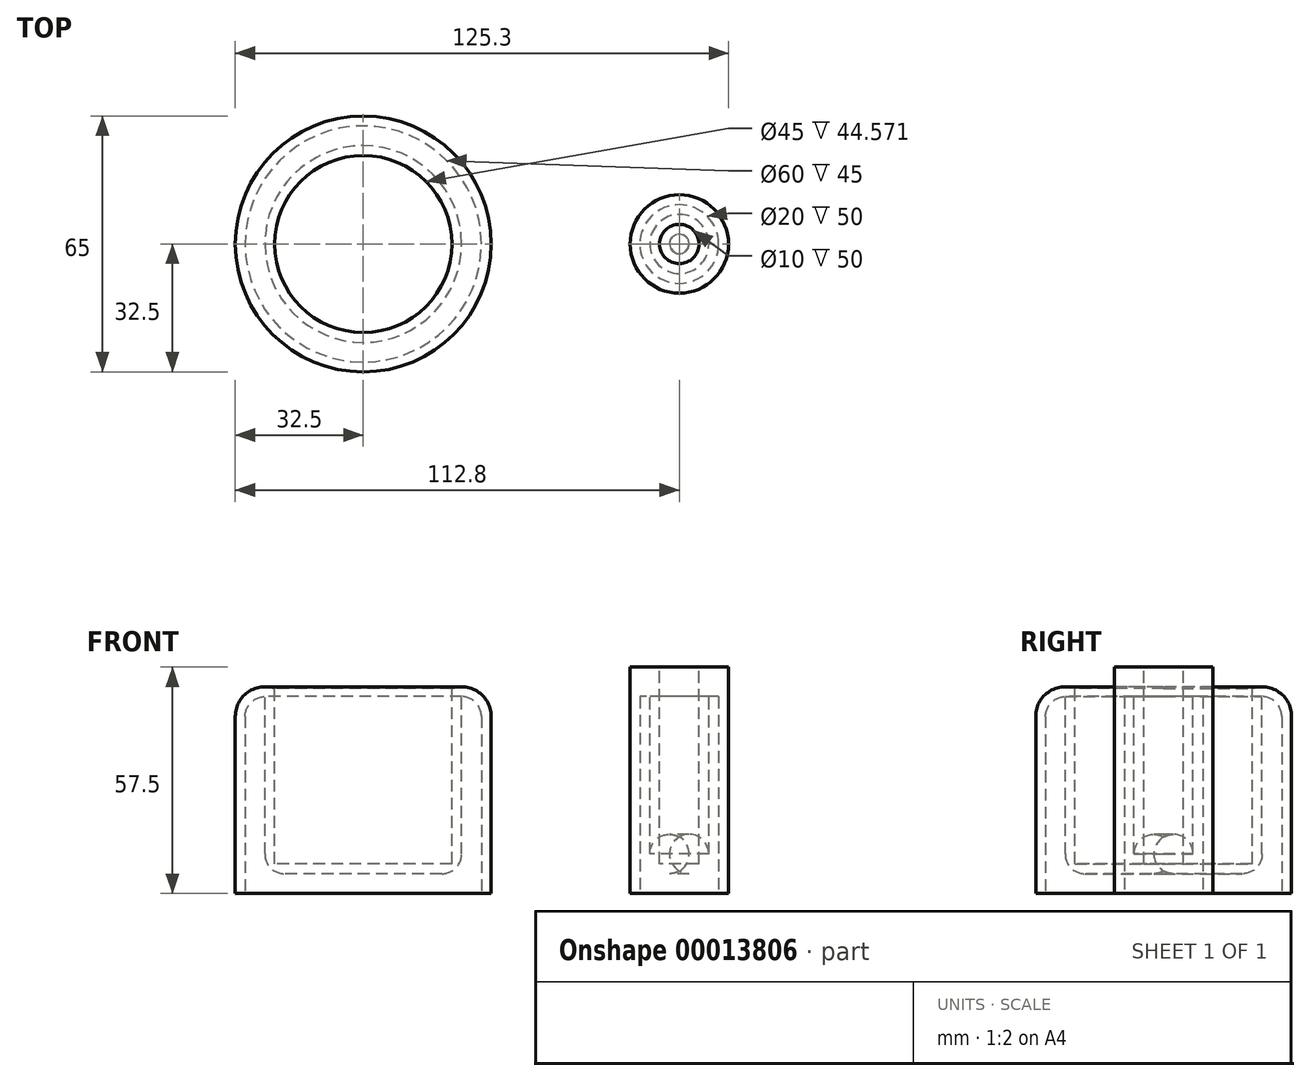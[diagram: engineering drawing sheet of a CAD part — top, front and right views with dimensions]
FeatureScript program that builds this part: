
annotation { "Feature Type Name" : "Feature", "Feature Type Description" : "" }
export const myFeature = defineFeature(function(context is Context, id is Id, definition is map)
    precondition{}
    {
        {
            var Q0;
            Q0=qCreatedBy(makeId("Top.planeOp"),FACE);
            var sketch = newSketch(context, id + "F0", { "sketchPlane" : qUnion([Q0])});
            skCircle(sketch, "E0", {"center": v(0, 0) * mm, "radius": 30 * mm});
            skCircle(sketch, "E1", {"center": v(80.3, 0) * mm, "radius": 10 * mm});
            skLineSegment(sketch, "E2", {"start": v(5.28, 29.53) * mm, "end": v(82.78, 9.69) * mm});
            skLineSegment(sketch, "E3", {"start": v(7.47, -29.05) * mm, "end": v(82.8, -9.68) * mm});
            skSolve(sketch);
        }
        {
            var Q0;
            Q0 = qSketchRegion(id + "F0", true);
            extrude(context, id + "F1", {"entities" : qUnion([Q0]), "depth" : 50 * mm});
        }
        {
            var Q0;
            Q0=makeQuery(id+"F1.opExtrude","CAP_FACE",FACE,{"disambiguationData":[OSD([sQuery(id+"F0.wireOp",EDGE,"E0"),sQuery(id+"F0.wireOp",EDGE,"E1"),sQuery(id+"F0.wireOp",EDGE,"E2"),sQuery(id+"F0.wireOp",EDGE,"E3")])],"isStart":false});
            var sketch = newSketch(context, id + "F2", { "sketchPlane" : qUnion([Q0])});
            skCircle(sketch, "E4", {"center": v(0, 0) * mm, "radius": 25 * mm});
            skCircle(sketch, "E5", {"center": v(80.3, 0) * mm, "radius": 7.5 * mm});
            skSolve(sketch);
        }
        {
            var Q0;
            Q0 = qSketchRegion(id + "F2", true);
            extrude(context, id + "F3", {"entities" : qUnion([Q0]), "operationType" : NewBodyOperationType.REMOVE, "oppositeDirection" : true, "depth" : 45 * mm});
        }
        {
            var Q0;
            Q0=makeQuery(id+"F1.opExtrude","CAP_EDGE",EDGE,{"disambiguationData":[OSD([sQuery(id+"F0.wireOp",EDGE,"E0")])],"isStart":false});
            var Q1;
            Q1=makeQuery(id+"F1.opExtrude","CAP_EDGE",EDGE,{"disambiguationData":[OSD([sQuery(id+"F0.wireOp",EDGE,"E2")])],"isStart":false});
            var Q2;
            Q2=makeQuery(id+"F3.boolean.opBoolean","COPY",EDGE,{"derivedFrom":makeQuery(id+"F3.opExtrude","CAP_EDGE",EDGE,{"disambiguationData":[OSD([sQuery(id+"F2.wireOp",EDGE,"E5")])],"isStart":true})});
            var Q3;
            Q3=makeQuery(id+"F3.boolean.opBoolean","COPY",EDGE,{"derivedFrom":makeQuery(id+"F3.opExtrude","CAP_EDGE",EDGE,{"disambiguationData":[OSD([sQuery(id+"F2.wireOp",EDGE,"E4")])],"isStart":true})});
            fillet(context, id + "F4", {"entities" : qUnion([Q0, Q1, Q2, Q3]), "radius" : 5 * mm, "tangentPropagation" : true, "allowEdgeOverflow" : false});
        }
        {
            var Q0;
            Q0=makeQuery(id+"F1.opExtrude","CAP_FACE",FACE,{"disambiguationData":[OSD([sQuery(id+"F0.wireOp",EDGE,"E0"),sQuery(id+"F0.wireOp",EDGE,"E1"),sQuery(id+"F0.wireOp",EDGE,"E2"),sQuery(id+"F0.wireOp",EDGE,"E3")])],"isStart":true});
            shell(context, id + "F5", {"entities" : qUnion([Q0]), "thickness" : 2.5 * mm, "oppositeDirection" : true});
        }
        {
            var Q0;
            {var subQ0=sQuery(id+"F2.wireOp",EDGE,"E4");Q0=makeQuery(id+"F5.opShell","OFFSET_EDGE",EDGE,{"disambiguationData":[OSD([subQ0]),TDD([makeQuery(id+"F3.boolean.opBoolean","COPY",EDGE,{"derivedFrom":makeQuery(id+"F3.opExtrude","CAP_EDGE",EDGE,{"disambiguationData":[OSD([subQ0])],"isStart":false})})])]});}
            var Q1;
            {var subQ0=sQuery(id+"F2.wireOp",EDGE,"E5");Q1=makeQuery(id+"F5.opShell","OFFSET_EDGE",EDGE,{"disambiguationData":[OSD([subQ0]),TDD([makeQuery(id+"F3.boolean.opBoolean","COPY",EDGE,{"derivedFrom":makeQuery(id+"F3.opExtrude","CAP_EDGE",EDGE,{"disambiguationData":[OSD([subQ0])],"isStart":false})})])]});}
            fillet(context, id + "F6", {"entities" : qUnion([Q0, Q1]), "radius" : 5 * mm, "tangentPropagation" : true, "allowEdgeOverflow" : false});
        }
        {
            var Q0;
            Q0=makeQuery(id+"F1.opExtrude","CAP_FACE",FACE,{"disambiguationData":[OSD([sQuery(id+"F0.wireOp",EDGE,"E0"),sQuery(id+"F0.wireOp",EDGE,"E1"),sQuery(id+"F0.wireOp",EDGE,"E2"),sQuery(id+"F0.wireOp",EDGE,"E3")])],"isStart":false});
            extrude(context, id + "F7", {"entities" : qUnion([Q0]), "operationType" : NewBodyOperationType.ADD, "depth" : 5 * mm});
        }
    });
